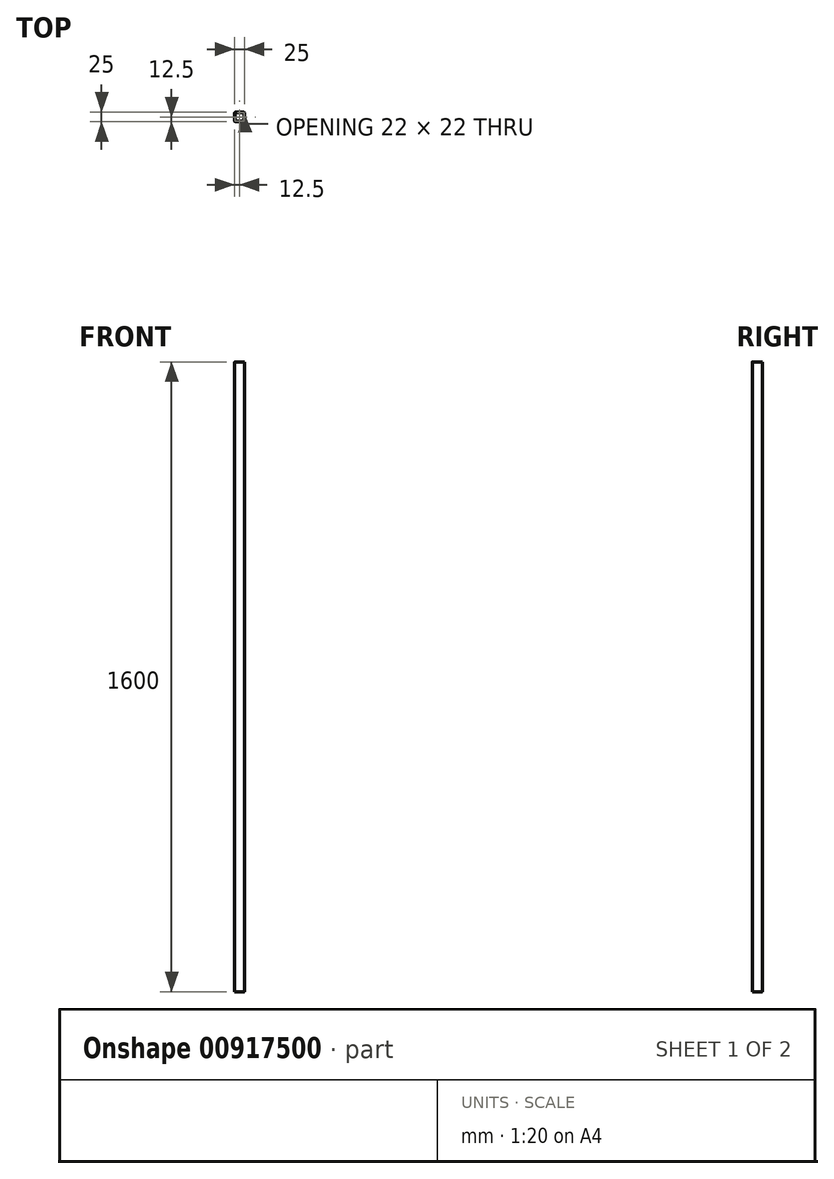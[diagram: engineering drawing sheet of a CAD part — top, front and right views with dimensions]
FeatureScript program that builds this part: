
annotation { "Feature Type Name" : "Feature", "Feature Type Description" : "" }
export const myFeature = defineFeature(function(context is Context, id is Id, definition is map)
    precondition{}
    {
        {
            var Q0;
            Q0=qCreatedBy(makeId("Top.planeOp"),FACE);
            var sketch = newSketch(context, id + "F0", { "sketchPlane" : qUnion([Q0])});
            skLineSegment(sketch, "E0.bottom", {"start": v(10, 12.5) * mm, "end": v(-10, 12.5) * mm});
            skLineSegment(sketch, "E0.top", {"start": v(10, -12.5) * mm, "end": v(-10, -12.5) * mm});
            skLineSegment(sketch, "E0.left", {"start": v(12.5, 10) * mm, "end": v(12.5, -10) * mm});
            skLineSegment(sketch, "E0.right", {"start": v(-12.5, 10) * mm, "end": v(-12.5, -10) * mm});
            skPoint(sketch, "E0.middle", {"position": v(0, 0) * mm});
            skPoint(sketch, "E1.visualSharp", {"position": v(-12.5, 12.5) * mm});
            skArc(sketch, "E1.filletArc", {"start": v(-10, 12.5) * mm, "mid": v(-11.77, 11.77) * mm, "end": v(-12.5, 10) * mm});
            skPoint(sketch, "E2.visualSharp", {"position": v(12.5, 12.5) * mm});
            skArc(sketch, "E2.filletArc", {"start": v(12.5, 10) * mm, "mid": v(11.77, 11.77) * mm, "end": v(10, 12.5) * mm});
            skPoint(sketch, "E3.visualSharp", {"position": v(12.5, -12.5) * mm});
            skArc(sketch, "E3.filletArc", {"start": v(10, -12.5) * mm, "mid": v(11.77, -11.77) * mm, "end": v(12.5, -10) * mm});
            skPoint(sketch, "E4.visualSharp", {"position": v(-12.5, -12.5) * mm});
            skArc(sketch, "E4.filletArc", {"start": v(-12.5, -10) * mm, "mid": v(-11.77, -11.77) * mm, "end": v(-10, -12.5) * mm});
            skLineSegment(sketch, "E5.0", {"start": v(10, -11) * mm, "end": v(-10, -11) * mm});
            skLineSegment(sketch, "E5.1", {"start": v(11, 11) * mm, "end": v(11, -10) * mm});
            skLineSegment(sketch, "E5.2", {"start": v(11, 11) * mm, "end": v(-10, 11) * mm});
            skLineSegment(sketch, "E5.3", {"start": v(-11, 10) * mm, "end": v(-11, -10) * mm});
            skPoint(sketch, "E6.visualSharp", {"position": v(-11, -11) * mm});
            skArc(sketch, "E6.filletArc", {"start": v(-11, -10) * mm, "mid": v(-10.7, -10.7) * mm, "end": v(-10, -11) * mm});
            skPoint(sketch, "E7.visualSharp", {"position": v(-11, 11) * mm});
            skArc(sketch, "E7.filletArc", {"start": v(-10, 11) * mm, "mid": v(-10.7, 10.7) * mm, "end": v(-11, 10) * mm});
            skPoint(sketch, "E8.visualSharp", {"position": v(11, -11) * mm});
            skArc(sketch, "E8.filletArc", {"start": v(10, -11) * mm, "mid": v(10.7, -10.7) * mm, "end": v(11, -10) * mm});
            skSolve(sketch);
        }
        {
            var Q0;
            Q0=qSketchRegion(id+"F0",true);
            extrude(context, id + "F1", {"entities" : qUnion([Q0]), "depth" : 1600 * mm, "offsetDistance" : 25 * mm});
        }
    });
